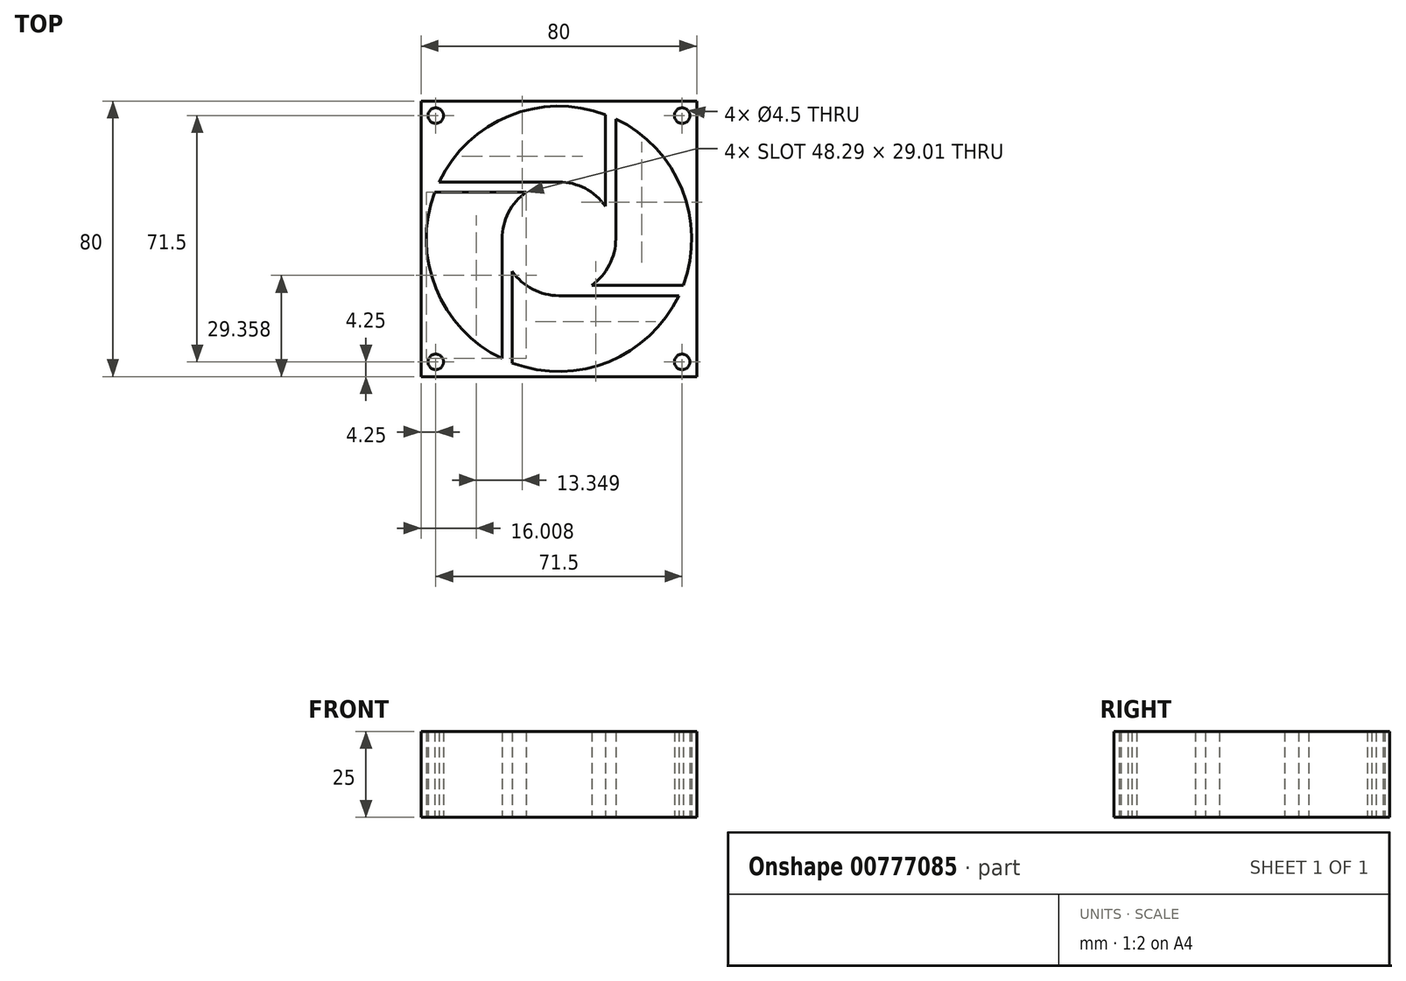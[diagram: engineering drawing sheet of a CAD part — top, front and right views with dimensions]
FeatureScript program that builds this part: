
annotation { "Feature Type Name" : "Feature", "Feature Type Description" : "" }
export const myFeature = defineFeature(function(context is Context, id is Id, definition is map)
    precondition{}
    {
        {
            var Q0;
            Q0=qCreatedBy(makeId("Top.planeOp"),FACE);
            var sketch = newSketch(context, id + "F0", { "sketchPlane" : qUnion([Q0])});
            skLineSegment(sketch, "E0.bottom", {"start": v(-40, 40) * mm, "end": v(40, 40) * mm});
            skLineSegment(sketch, "E0.top", {"start": v(-40, -40) * mm, "end": v(40, -40) * mm});
            skLineSegment(sketch, "E0.left", {"start": v(-40, 40) * mm, "end": v(-40, -40) * mm});
            skLineSegment(sketch, "E0.right", {"start": v(40, 40) * mm, "end": v(40, -40) * mm});
            skLineSegment(sketch, "E1", {"start": v(-40, 40) * mm, "end": v(40, -40) * mm, "construction": true});
            skCircle(sketch, "E2", {"center": v(0, 0) * mm, "radius": 38.5 * mm});
            skLineSegment(sketch, "E3", {"start": v(-40, -40) * mm, "end": v(40, 40) * mm, "construction": true});
            skLineSegment(sketch, "E4.bottom", {"start": v(-35.75, 35.75) * mm, "end": v(35.75, 35.75) * mm, "construction": true});
            skLineSegment(sketch, "E4.top", {"start": v(-35.75, -35.75) * mm, "end": v(35.75, -35.75) * mm, "construction": true});
            skLineSegment(sketch, "E4.left", {"start": v(-35.75, 35.75) * mm, "end": v(-35.75, -35.75) * mm, "construction": true});
            skLineSegment(sketch, "E4.right", {"start": v(35.75, 35.75) * mm, "end": v(35.75, -35.75) * mm, "construction": true});
            skCircle(sketch, "E5", {"center": v(35.75, 35.75) * mm, "radius": 2.25 * mm});
            skCircle(sketch, "E6", {"center": v(-35.75, 35.75) * mm, "radius": 2.25 * mm});
            skCircle(sketch, "E7", {"center": v(-35.75, -35.75) * mm, "radius": 2.25 * mm});
            skCircle(sketch, "E8", {"center": v(35.75, -35.75) * mm, "radius": 2.25 * mm});
            skSolve(sketch);
        }
        {
            var Q0;
            Q0=qSketchRegion(id+"F0",true);
            extrude(context, id + "F1", {"entities" : qUnion([Q0]), "depth" : 25 * mm});
        }
        {
            var Q0;
            Q0=qCreatedBy(makeId("Top.planeOp"),FACE);
            var sketch = newSketch(context, id + "F2", { "sketchPlane" : qUnion([Q0])});
            skCircle(sketch, "E9", {"center": v(0, 0) * mm, "radius": 16.5 * mm});
            skLineSegment(sketch, "E10.bottom", {"start": v(0, 13.5) * mm, "end": v(-36.06, 13.5) * mm});
            skLineSegment(sketch, "E10.top", {"start": v(0, 16.5) * mm, "end": v(-36.06, 16.5) * mm});
            skLineSegment(sketch, "E10.left", {"start": v(0, 13.5) * mm, "end": v(0, 16.5) * mm});
            skLineSegment(sketch, "E10.right", {"start": v(-36.06, 13.5) * mm, "end": v(-36.06, 16.5) * mm});
            skCircle(sketch, "E11.0", {"center": v(0, 0) * mm, "radius": 38.5 * mm});
            skLineSegment(sketch, "E12.1.0", {"start": v(-16.5, 0) * mm, "end": v(-16.5, -36.06) * mm});
            skLineSegment(sketch, "E12.1.1", {"start": v(-13.5, 0) * mm, "end": v(-13.5, -36.06) * mm});
            skLineSegment(sketch, "E12.1.2", {"start": v(-13.5, 0) * mm, "end": v(-16.5, 0) * mm});
            skLineSegment(sketch, "E12.1.3", {"start": v(-13.5, -36.06) * mm, "end": v(-16.5, -36.06) * mm});
            skLineSegment(sketch, "E12.2.0", {"start": v(0, -16.5) * mm, "end": v(36.06, -16.5) * mm});
            skLineSegment(sketch, "E12.2.1", {"start": v(0, -13.5) * mm, "end": v(36.06, -13.5) * mm});
            skLineSegment(sketch, "E12.2.2", {"start": v(0, -13.5) * mm, "end": v(0, -16.5) * mm});
            skLineSegment(sketch, "E12.2.3", {"start": v(36.06, -13.5) * mm, "end": v(36.06, -16.5) * mm});
            skLineSegment(sketch, "E12.3.0", {"start": v(16.5, 0) * mm, "end": v(16.5, 36.06) * mm});
            skLineSegment(sketch, "E12.3.1", {"start": v(13.5, 0) * mm, "end": v(13.5, 36.06) * mm});
            skLineSegment(sketch, "E12.3.2", {"start": v(13.5, 0) * mm, "end": v(16.5, 0) * mm});
            skLineSegment(sketch, "E12.3.3", {"start": v(13.5, 36.06) * mm, "end": v(16.5, 36.06) * mm});
            skSolve(sketch);
        }
        {
            var Q0;
            {var subQ12=sQuery(id+"F2.wireOp",EDGE,"E10.left");Q0=makeQuery(id+"F2.imprint","IMPRINT",FACE,{"disambiguationData":[TD([[makeQuery(id+"F2.imprint","IMPRINT",EDGE,{"derivedFrom":subQ12}),-1.0]])]});}
            var Q1;
            {var subQ0=sQuery(id+"F2.wireOp",EDGE,"E12.3.1");var subQ1=sQuery(id+"F2.wireOp",EDGE,"E9");var subQ2=makeQuery(id+"F2.imprint","INTERSECT",VERTEX,{"derivedFrom":[subQ1,subQ0]});Q1=makeQuery(id+"F2.imprint","IMPRINT",FACE,{"disambiguationData":[TD([[makeQuery(id+"F2.imprint","IMPRINT",EDGE,{"disambiguationData":[TD([[subQ2,1.0]])],"derivedFrom":subQ1}),-1.0]])]});}
            var Q2;
            {var subQ0=sQuery(id+"F2.wireOp",EDGE,"E12.3.2");Q2=makeQuery(id+"F2.imprint","IMPRINT",FACE,{"disambiguationData":[TD([[makeQuery(id+"F2.imprint","IMPRINT",EDGE,{"derivedFrom":subQ0}),1.0]])]});}
            var Q3;
            {var subQ0=sQuery(id+"F2.wireOp",EDGE,"E10.left");Q3=makeQuery(id+"F2.imprint","IMPRINT",FACE,{"disambiguationData":[TD([[makeQuery(id+"F2.imprint","IMPRINT",EDGE,{"derivedFrom":subQ0}),1.0]])]});}
            var Q4;
            {var subQ3=sQuery(id+"F2.wireOp",EDGE,"E10.bottom");var subQ5=sQuery(id+"F2.wireOp",EDGE,"E9");var subQ7=makeQuery(id+"F2.imprint","INTERSECT",VERTEX,{"derivedFrom":[subQ5,subQ3]});Q4=makeQuery(id+"F2.imprint","IMPRINT",FACE,{"disambiguationData":[TD([[makeQuery(id+"F2.imprint","IMPRINT",EDGE,{"disambiguationData":[TD([[subQ7,1.0]])],"derivedFrom":subQ5}),-1.0]])]});}
            var Q5;
            {var subQ0=sQuery(id+"F2.wireOp",EDGE,"E12.1.2");Q5=makeQuery(id+"F2.imprint","IMPRINT",FACE,{"disambiguationData":[TD([[makeQuery(id+"F2.imprint","IMPRINT",EDGE,{"derivedFrom":subQ0}),1.0]])]});}
            var Q6;
            {var subQ0=sQuery(id+"F2.wireOp",EDGE,"E12.1.1");var subQ1=sQuery(id+"F2.wireOp",EDGE,"E9");var subQ2=makeQuery(id+"F2.imprint","INTERSECT",VERTEX,{"derivedFrom":[subQ1,subQ0]});Q6=makeQuery(id+"F2.imprint","IMPRINT",FACE,{"disambiguationData":[TD([[makeQuery(id+"F2.imprint","IMPRINT",EDGE,{"disambiguationData":[TD([[subQ2,1.0]])],"derivedFrom":subQ1}),-1.0]])]});}
            var Q7;
            {var subQ0=sQuery(id+"F2.wireOp",EDGE,"E12.2.2");Q7=makeQuery(id+"F2.imprint","IMPRINT",FACE,{"disambiguationData":[TD([[makeQuery(id+"F2.imprint","IMPRINT",EDGE,{"derivedFrom":subQ0}),1.0]])]});}
            var Q8;
            {var subQ0=sQuery(id+"F2.wireOp",EDGE,"E12.2.1");var subQ1=sQuery(id+"F2.wireOp",EDGE,"E9");var subQ2=makeQuery(id+"F2.imprint","INTERSECT",VERTEX,{"derivedFrom":[subQ1,subQ0]});Q8=makeQuery(id+"F2.imprint","IMPRINT",FACE,{"disambiguationData":[TD([[makeQuery(id+"F2.imprint","IMPRINT",EDGE,{"disambiguationData":[TD([[subQ2,1.0]])],"derivedFrom":subQ1}),-1.0]])]});}
            extrude(context, id + "F3", {"entities" : qUnion([Q0, Q1, Q2, Q3, Q4, Q5, Q6, Q7, Q8]), "operationType" : NewBodyOperationType.ADD, "depth" : 25 * mm, "offsetDistance" : 25 * mm});
        }
    });
